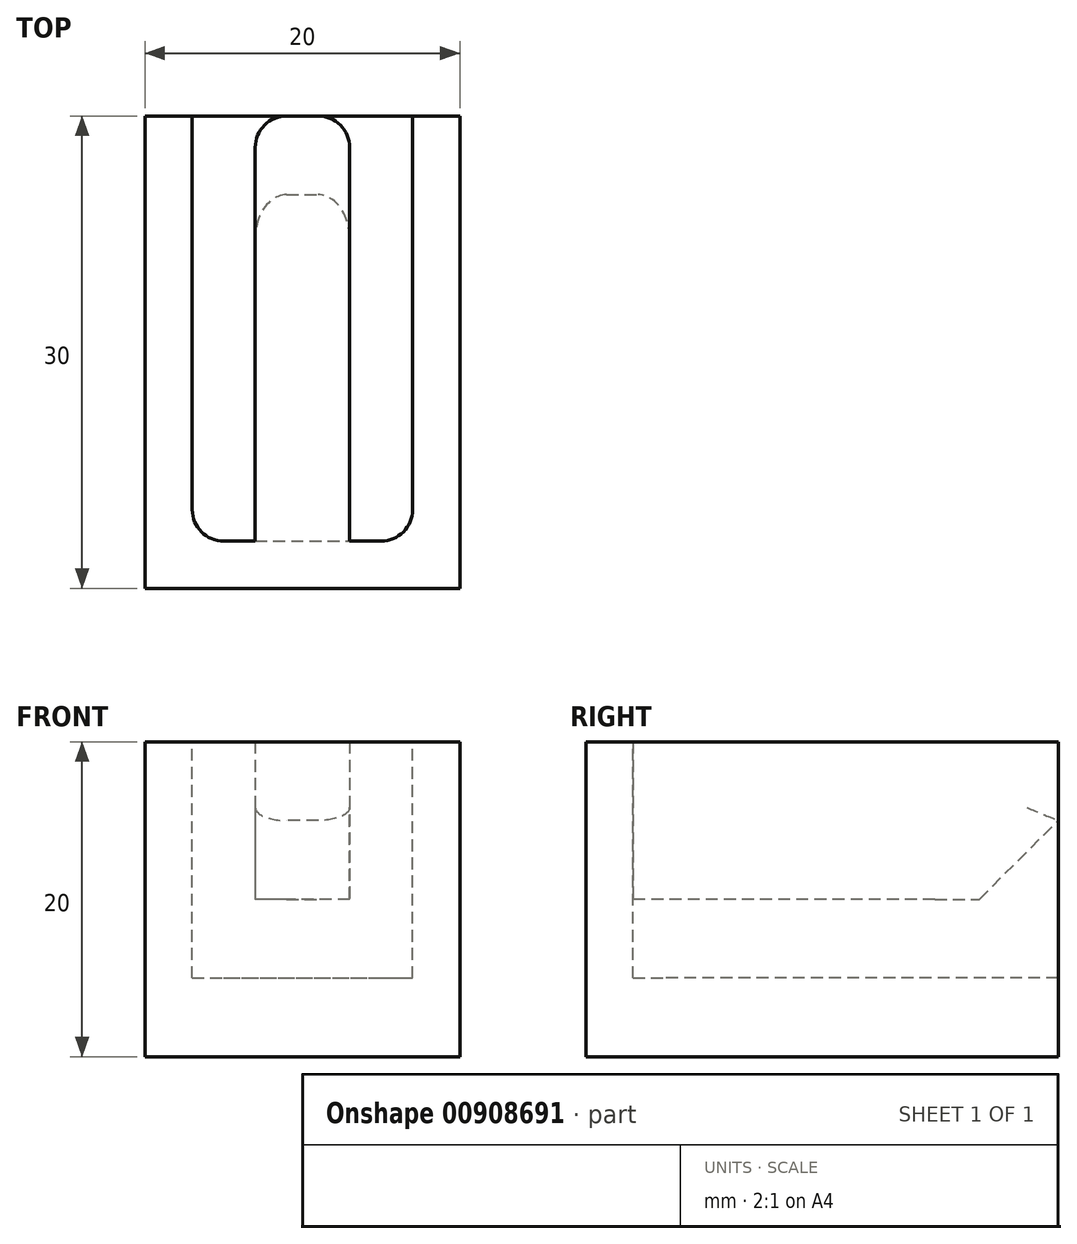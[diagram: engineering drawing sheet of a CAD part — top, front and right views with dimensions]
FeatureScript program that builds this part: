
annotation { "Feature Type Name" : "Feature", "Feature Type Description" : "" }
export const myFeature = defineFeature(function(context is Context, id is Id, definition is map)
    precondition{}
    {
        {
            var Q0;
            Q0=qCreatedBy(makeId("Top.planeOp"),FACE);
            var sketch = newSketch(context, id + "F0", { "sketchPlane" : qUnion([Q0])});
            skLineSegment(sketch, "E0", {"start": v(0, 0) * mm, "end": v(50, 0) * mm, "construction": true});
            skLineSegment(sketch, "E1", {"start": v(0, 0) * mm, "end": v(0, 60) * mm, "construction": true});
            skLineSegment(sketch, "E2", {"start": v(50, 60) * mm, "end": v(0, 10) * mm, "construction": true});
            skLineSegment(sketch, "E3.bottom", {"start": v(40, 75) * mm, "end": v(60, 75) * mm});
            skLineSegment(sketch, "E3.top", {"start": v(40, 45) * mm, "end": v(60, 45) * mm});
            skLineSegment(sketch, "E3.left", {"start": v(40, 75) * mm, "end": v(40, 45) * mm});
            skLineSegment(sketch, "E3.right", {"start": v(60, 75) * mm, "end": v(60, 45) * mm});
            skLineSegment(sketch, "E4", {"start": v(60, 45) * mm, "end": v(40, 75) * mm, "construction": true});
            skPoint(sketch, "E5", {"position": v(50, 60) * mm});
            skSolve(sketch);
        }
        {
            var Q0;
            Q0 = qSketchRegion(id + "F0", true);
            extrude(context, id + "F1", {"entities" : qUnion([Q0]), "depth" : 20 * mm, "offsetDistance" : 25 * mm});
        }
        {
            var Q0;
            Q0=makeQuery(id+"F1.opExtrude","CAP_FACE",FACE,{"disambiguationData":[OSD([sQuery(id+"F0.wireOp",EDGE,"E3.bottom"),sQuery(id+"F0.wireOp",EDGE,"E3.top"),sQuery(id+"F0.wireOp",EDGE,"E3.left"),sQuery(id+"F0.wireOp",EDGE,"E3.right")])],"isStart":false});
            var sketch = newSketch(context, id + "F2", { "sketchPlane" : qUnion([Q0])});
            skLineSegment(sketch, "E6.bottom", {"start": v(43, 75) * mm, "end": v(57, 75) * mm});
            skLineSegment(sketch, "E6.top", {"start": v(43, 48) * mm, "end": v(57, 48) * mm});
            skLineSegment(sketch, "E6.left", {"start": v(43, 75) * mm, "end": v(43, 48) * mm});
            skLineSegment(sketch, "E6.right", {"start": v(57, 75) * mm, "end": v(57, 48) * mm});
            skSolve(sketch);
        }
        {
            var Q0;
            Q0 = qSketchRegion(id + "F2", true);
            extrude(context, id + "F3", {"entities" : qUnion([Q0]), "operationType" : NewBodyOperationType.REMOVE, "oppositeDirection" : true, "depth" : 15 * mm, "offsetDistance" : 25 * mm});
        }
        {
            var Q0;
            Q0=makeQuery(id+"F3.boolean.opBoolean","COPY",FACE,{"derivedFrom":makeQuery(id+"F3.opExtrude","SWEPT_FACE",FACE,{"disambiguationData":[OSD([sQuery(id+"F2.wireOp",EDGE,"E6.top")])]})});
            var sketch = newSketch(context, id + "F4", { "sketchPlane" : qUnion([Q0])});
            skLineSegment(sketch, "E7.bottom", {"start": v(-53, 20) * mm, "end": v(-47, 20) * mm});
            skLineSegment(sketch, "E7.top", {"start": v(-53, 10) * mm, "end": v(-47, 10) * mm});
            skLineSegment(sketch, "E7.left", {"start": v(-53, 20) * mm, "end": v(-53, 10) * mm});
            skLineSegment(sketch, "E7.right", {"start": v(-47, 20) * mm, "end": v(-47, 10) * mm});
            skLineSegment(sketch, "E8", {"start": v(-57, 20) * mm, "end": v(-53, 20) * mm, "construction": true});
            skLineSegment(sketch, "E9", {"start": v(-47, 20) * mm, "end": v(-43, 20) * mm, "construction": true});
            skSolve(sketch);
        }
        {
            var Q0;
            Q0 = qSketchRegion(id + "F4", true);
            var Q1;
            Q1=makeQuery(id+"F1.opExtrude","SWEPT_FACE",FACE,{"disambiguationData":[OSD([sQuery(id+"F0.wireOp",EDGE,"E3.bottom")])]});
            extrude(context, id + "F5", {"entities" : qUnion([Q0]), "operationType" : NewBodyOperationType.ADD, "endBound" : BoundingType.UP_TO_SURFACE, "depth" : 25 * mm, "endBoundEntityFace" : qUnion([Q1]), "offsetDistance" : 25 * mm});
        }
        {
            var Q0;
            Q0=makeQuery(id+"F5.opExtrude","CAP_EDGE",EDGE,{"disambiguationData":[OSD([sQuery(id+"F4.wireOp",EDGE,"E7.top")])],"isStart":false});
            chamfer(context, id + "F6", {"entities" : qUnion([Q0]), "width" : 5 * mm, "tangentPropagation" : true});
        }
        {
            var Q0;
            Q0=makeQuery(id+"F3.boolean.opBoolean","COPY",EDGE,{"derivedFrom":makeQuery(id+"F3.opExtrude","SWEPT_EDGE",EDGE,{"disambiguationData":[OSD([sQuery(id+"F2.wireOp",EDGE,"E6.top"),sQuery(id+"F2.wireOp",EDGE,"E6.left")])]})});
            var Q1;
            Q1=makeQuery(id+"F5.opExtrude","CAP_EDGE",EDGE,{"disambiguationData":[OSD([sQuery(id+"F4.wireOp",EDGE,"E7.right")])],"isStart":true});
            var Q2;
            Q2=makeQuery(id+"F3.boolean.opBoolean","COPY",EDGE,{"derivedFrom":makeQuery(id+"F3.opExtrude","SWEPT_EDGE",EDGE,{"disambiguationData":[OSD([sQuery(id+"F2.wireOp",EDGE,"E6.top"),sQuery(id+"F2.wireOp",EDGE,"E6.right")])]})});
            var Q3;
            Q3=makeQuery(id+"F5.opExtrude","CAP_EDGE",EDGE,{"disambiguationData":[OSD([sQuery(id+"F4.wireOp",EDGE,"E7.left")])],"isStart":true});
            var Q4;
            Q4=makeQuery(id+"F5.opExtrude","CAP_EDGE",EDGE,{"disambiguationData":[OSD([sQuery(id+"F4.wireOp",EDGE,"E7.left")])],"isStart":false});
            var Q5;
            Q5=makeQuery(id+"F5.opExtrude","CAP_EDGE",EDGE,{"disambiguationData":[OSD([sQuery(id+"F4.wireOp",EDGE,"E7.right")])],"isStart":false});
            var Q6;
            Q6=makeQuery(id+"F6.opChamfer","BLEND_EDGE",EDGE,{"blendedFrom":[makeQuery(id+"F5.opExtrude","CAP_EDGE",EDGE,{"disambiguationData":[OSD([sQuery(id+"F4.wireOp",EDGE,"E7.top")])],"isStart":false}),makeQuery(id+"F5.opExtrude","SWEPT_FACE",FACE,{"disambiguationData":[OSD([sQuery(id+"F4.wireOp",EDGE,"E7.right")])]})],"blendedInto":[makeQuery(id+"F5.opExtrude","SWEPT_FACE",FACE,{"disambiguationData":[OSD([sQuery(id+"F4.wireOp",EDGE,"E7.right")])]})]});
            var Q7;
            Q7=makeQuery(id+"F6.opChamfer","BLEND_EDGE",EDGE,{"blendedFrom":[makeQuery(id+"F5.opExtrude","CAP_EDGE",EDGE,{"disambiguationData":[OSD([sQuery(id+"F4.wireOp",EDGE,"E7.top")])],"isStart":false}),makeQuery(id+"F5.opExtrude","SWEPT_FACE",FACE,{"disambiguationData":[OSD([sQuery(id+"F4.wireOp",EDGE,"E7.left")])]})],"blendedInto":[makeQuery(id+"F5.opExtrude","SWEPT_FACE",FACE,{"disambiguationData":[OSD([sQuery(id+"F4.wireOp",EDGE,"E7.left")])]})]});
            fillet(context, id + "F7", {"entities" : qUnion([Q0, Q1, Q2, Q3, Q4, Q5, Q6, Q7]), "radius" : 2 * mm, "tangentPropagation" : true, "allowEdgeOverflow" : false});
        }
    });
